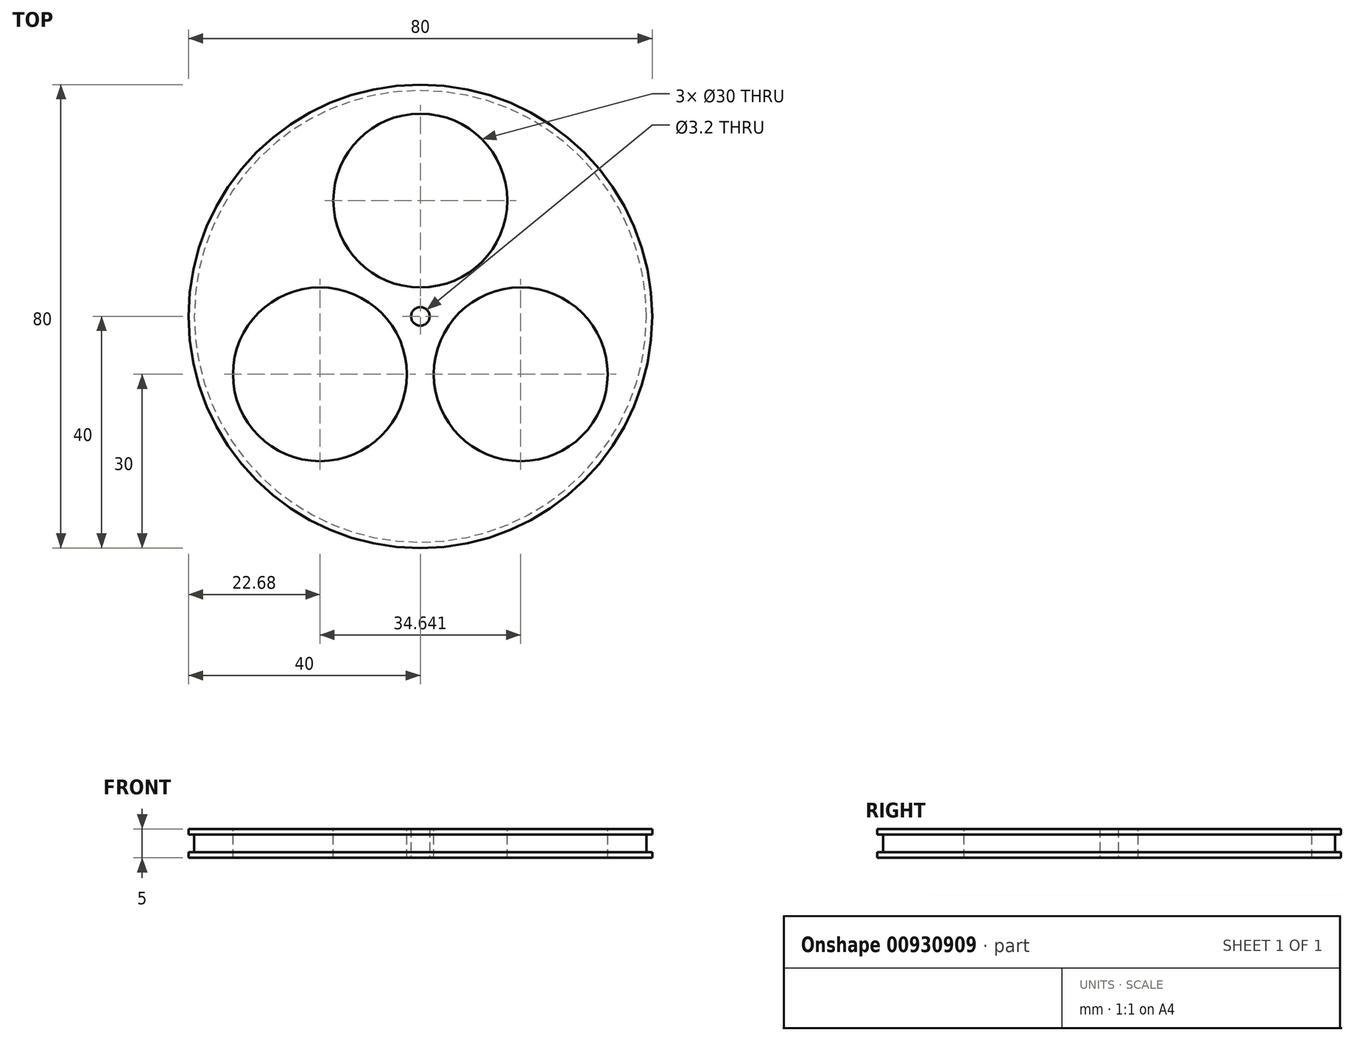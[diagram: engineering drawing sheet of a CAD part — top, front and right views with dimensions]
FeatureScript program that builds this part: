
annotation { "Feature Type Name" : "Feature", "Feature Type Description" : "" }
export const myFeature = defineFeature(function(context is Context, id is Id, definition is map)
    precondition{}
    {
        {
            var Q0;
            Q0=qCreatedBy(makeId("Top.planeOp"),FACE);
            var sketch = newSketch(context, id + "F0", { "sketchPlane" : qUnion([Q0])});
            skCircle(sketch, "E0", {"center": v(0, 0) * mm, "radius": 40 * mm});
            skCircle(sketch, "E1", {"center": v(0, 0) * mm, "radius": 1.6 * mm});
            skPoint(sketch, "E2.0.midPoint", {"position": v(30, 0) * mm});
            skSolve(sketch);
        }
        {
            var Q0;
            Q0 = qSketchRegion(id + "F0", true);
            extrude(context, id + "F1", {"entities" : qUnion([Q0]), "depth" : 5 * mm, "offsetDistance" : 25 * mm});
        }
        {
            var Q0;
            Q0=qCreatedBy(makeId("Right.planeOp"),FACE);
            var sketch = newSketch(context, id + "F2", { "sketchPlane" : qUnion([Q0])});
            skLineSegment(sketch, "E3.bottom", {"start": v(40, 4) * mm, "end": v(39, 4) * mm});
            skLineSegment(sketch, "E3.top", {"start": v(40, 1) * mm, "end": v(39, 1) * mm});
            skLineSegment(sketch, "E3.left", {"start": v(40, 4) * mm, "end": v(40, 1) * mm});
            skLineSegment(sketch, "E3.right", {"start": v(39, 4) * mm, "end": v(39, 1) * mm});
            skLineSegment(sketch, "E4", {"start": v(40, 5) * mm, "end": v(40, 0) * mm, "construction": true});
            skLineSegment(sketch, "E5", {"start": v(-40, 0) * mm, "end": v(-40, 5) * mm});
            skSolve(sketch);
        }
        {
            var Q0;
            Q0 = qSketchRegion(id + "F2", true);
            var Q1;
            Q1=makeQuery(id+"F1.opExtrude","CAP_EDGE",EDGE,{"disambiguationData":[OSD([sQuery(id+"F0.wireOp",EDGE,"E0")])],"isStart":false});
            revolve(context, id + "F3", {"operationType" : NewBodyOperationType.REMOVE, "surfaceOperationType" : NewSurfaceOperationType.NEW, "entities" : qUnion([Q0]), "axis" : qUnion([Q1]), "revolveType" : RevolveType.FULL, "oppositeDirection" : true});
        }
        {
            var Q0;
            Q0=makeQuery(id+"F1.opExtrude","CAP_FACE",FACE,{"disambiguationData":[OSD([sQuery(id+"F0.wireOp",EDGE,"E0"),sQuery(id+"F0.wireOp",EDGE,"E1")])],"isStart":false});
            var sketch = newSketch(context, id + "F4", { "sketchPlane" : qUnion([Q0])});
            skCircle(sketch, "E6", {"center": v(0, 20) * mm, "radius": 15 * mm});
            skCircle(sketch, "E7.1.0", {"center": v(-17.32, -10) * mm, "radius": 15 * mm});
            skCircle(sketch, "E7.2.0", {"center": v(17.32, -10) * mm, "radius": 15 * mm});
            skPoint(sketch, "E7.center", {"position": v(0, 0) * mm});
            skLineSegment(sketch, "E8", {"start": v(-40, 0) * mm, "end": v(40, 0) * mm, "construction": true});
            skSolve(sketch);
        }
        {
            var Q0;
            Q0 = qSketchRegion(id + "F4", true);
            extrude(context, id + "F5", {"entities" : qUnion([Q0]), "operationType" : NewBodyOperationType.REMOVE, "oppositeDirection" : true, "depth" : 25 * mm, "offsetDistance" : 25 * mm});
        }
    });
